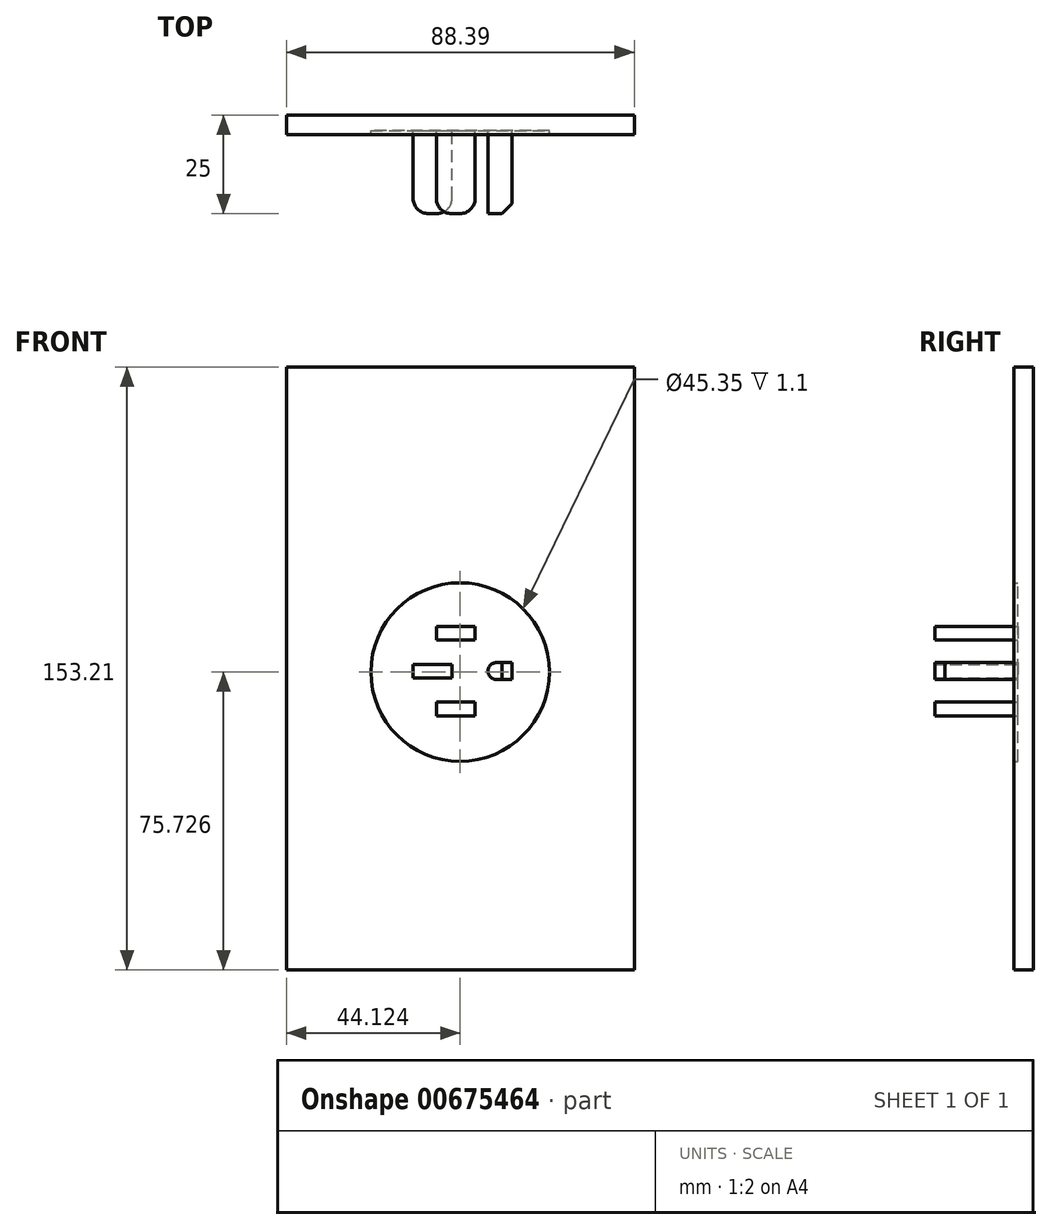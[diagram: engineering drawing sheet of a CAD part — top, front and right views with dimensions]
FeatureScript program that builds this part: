
annotation { "Feature Type Name" : "Feature", "Feature Type Description" : "" }
export const myFeature = defineFeature(function(context is Context, id is Id, definition is map)
    precondition{}
    {
        {
            var Q0;
            Q0=qCreatedBy(makeId("Front.planeOp"),FACE);
            var sketch = newSketch(context, id + "F0", { "sketchPlane" : qUnion([Q0])});
            skLineSegment(sketch, "E0.bottom", {"start": v(-39.21, 77.32) * mm, "end": v(49.18, 77.32) * mm});
            skLineSegment(sketch, "E0.top", {"start": v(-39.21, -75.89) * mm, "end": v(49.18, -75.89) * mm});
            skLineSegment(sketch, "E0.left", {"start": v(-39.21, 77.32) * mm, "end": v(-39.21, -75.89) * mm});
            skLineSegment(sketch, "E0.right", {"start": v(49.18, 77.32) * mm, "end": v(49.18, -75.89) * mm});
            skCircle(sketch, "E1", {"center": v(4.91, -0.16) * mm, "radius": 22.67 * mm});
            skLineSegment(sketch, "E2.bottom", {"start": v(-1.14, -11.26) * mm, "end": v(-1.14, -7.82) * mm});
            skLineSegment(sketch, "E2.top", {"start": v(8.73, -11.26) * mm, "end": v(8.73, -7.82) * mm});
            skLineSegment(sketch, "E2.left", {"start": v(-1.14, -11.26) * mm, "end": v(8.73, -11.26) * mm});
            skLineSegment(sketch, "E2.right", {"start": v(-1.14, -7.82) * mm, "end": v(8.73, -7.82) * mm});
            skLineSegment(sketch, "E3.MirrorCS", {"start": v(-7.02, -1.65) * mm, "end": v(2.85, -1.65) * mm});
            skLineSegment(sketch, "E4.MirrorCS", {"start": v(-1.14, 7.96) * mm, "end": v(8.73, 7.96) * mm});
            skLineSegment(sketch, "E5.MirrorCS", {"start": v(-1.14, 11.4) * mm, "end": v(-1.14, 7.96) * mm});
            skLineSegment(sketch, "E6.MirrorCS", {"start": v(-1.14, 11.4) * mm, "end": v(8.73, 11.4) * mm});
            skLineSegment(sketch, "E7.MirrorCS", {"start": v(8.73, 11.4) * mm, "end": v(8.73, 7.96) * mm});
            skLineSegment(sketch, "E8.MirrorCS", {"start": v(-7.02, 1.79) * mm, "end": v(2.85, 1.79) * mm});
            skLineSegment(sketch, "E9", {"start": v(-7.02, -1.65) * mm, "end": v(-7.02, 1.79) * mm});
            skLineSegment(sketch, "E10", {"start": v(2.85, -1.65) * mm, "end": v(2.85, 1.79) * mm});
            skLineSegment(sketch, "E11.bottom", {"start": v(18.11, -2.07) * mm, "end": v(18.11, 2.22) * mm});
            skLineSegment(sketch, "E11.left", {"start": v(18.11, -2.07) * mm, "end": v(14.12, -2.07) * mm});
            skLineSegment(sketch, "E11.right", {"start": v(18.11, 2.22) * mm, "end": v(14.12, 2.22) * mm});
            skArc(sketch, "E12", {"start": v(14.12, 2.22) * mm, "mid": v(11.97, 0.07) * mm, "end": v(14.12, -2.07) * mm});
            skSolve(sketch);
        }
        {
            var Q0;
            Q0=makeQuery(id+"F0.imprint","IMPRINT",FACE,{"disambiguationData":[TD([[makeQuery(id+"F0.imprint","IMPRINT",EDGE,{"derivedFrom":sQuery(id+"F0.wireOp",EDGE,"E0.bottom")}),-1.0]])]});
            extrude(context, id + "F1", {"entities" : qUnion([Q0]), "depth" : 5 * mm, "offsetDistance" : 25 * mm});
        }
        {
            var Q0;
            Q0=makeQuery(id+"F0.imprint","IMPRINT",FACE,{"disambiguationData":[TD([[makeQuery(id+"F0.imprint","IMPRINT",EDGE,{"derivedFrom":sQuery(id+"F0.wireOp",EDGE,"d919d92a-e6f7-40fd-a133-639b44a9ff66.bottom")}),1.0]])]});
            var Q1;
            Q1=makeQuery(id+"F0.imprint","IMPRINT",FACE,{"disambiguationData":[TD([[makeQuery(id+"F0.imprint","IMPRINT",EDGE,{"derivedFrom":sQuery(id+"F0.wireOp",EDGE,"E1")}),1.0]])]});
            extrude(context, id + "F2", {"entities" : qUnion([Q0, Q1]), "operationType" : NewBodyOperationType.ADD, "depth" : 3.9 * mm, "offsetDistance" : 25 * mm});
        }
        {
            var Q0;
            Q0=makeQuery(id+"F0.imprint","IMPRINT",FACE,{"disambiguationData":[TD([[makeQuery(id+"F0.imprint","IMPRINT",EDGE,{"derivedFrom":sQuery(id+"F0.wireOp",EDGE,"92b3ff77-899c-4692-b596-e14258b6b191")}),1.0]])]});
            var Q1;
            Q1=makeQuery(id+"F0.imprint","IMPRINT",FACE,{"disambiguationData":[TD([[makeQuery(id+"F0.imprint","IMPRINT",EDGE,{"derivedFrom":sQuery(id+"F0.wireOp",EDGE,"f2a1dbcd-aa5e-4286-995f-65eb86ff6750.MirrorCS")}),-1.0]])]});
            var Q2;
            Q2=makeQuery(id+"F0.imprint","IMPRINT",FACE,{"disambiguationData":[TD([[makeQuery(id+"F0.imprint","IMPRINT",EDGE,{"derivedFrom":sQuery(id+"F0.wireOp",EDGE,"d919d92a-e6f7-40fd-a133-639b44a9ff66.bottom")}),-1.0]])]});
            var Q3;
            Q3=makeQuery(id+"F0.imprint","IMPRINT",FACE,{"disambiguationData":[TD([[makeQuery(id+"F0.imprint","IMPRINT",EDGE,{"derivedFrom":sQuery(id+"F0.wireOp",EDGE,"E2.bottom")}),-1.0]])]});
            var Q4;
            Q4=makeQuery(id+"F0.imprint","IMPRINT",FACE,{"disambiguationData":[TD([[makeQuery(id+"F0.imprint","IMPRINT",EDGE,{"derivedFrom":sQuery(id+"F0.wireOp",EDGE,"E3.MirrorCS")}),1.0]])]});
            var Q5;
            Q5=makeQuery(id+"F0.imprint","IMPRINT",FACE,{"disambiguationData":[TD([[makeQuery(id+"F0.imprint","IMPRINT",EDGE,{"derivedFrom":sQuery(id+"F0.wireOp",EDGE,"E4.MirrorCS")}),1.0]])]});
            var Q6;
            Q6=makeQuery(id+"F0.imprint","IMPRINT",FACE,{"disambiguationData":[TD([[makeQuery(id+"F0.imprint","IMPRINT",EDGE,{"derivedFrom":sQuery(id+"F0.wireOp",EDGE,"E11.bottom")}),1.0]])]});
            extrude(context, id + "F3", {"entities" : qUnion([Q0, Q1, Q2, Q3, Q4, Q5, Q6]), "operationType" : NewBodyOperationType.ADD, "depth" : 25 * mm, "offsetDistance" : 25 * mm});
        }
        {
            var Q0;
            Q0=makeQuery(id+"F3.opExtrude","CAP_EDGE",EDGE,{"disambiguationData":[OSD([sQuery(id+"F0.wireOp",EDGE,"E2.bottom")])],"isStart":false});
            var Q1;
            Q1=makeQuery(id+"F3.opExtrude","CAP_EDGE",EDGE,{"disambiguationData":[OSD([sQuery(id+"F0.wireOp",EDGE,"E2.top")])],"isStart":false});
            var Q2;
            Q2=makeQuery(id+"F3.opExtrude","CAP_EDGE",EDGE,{"disambiguationData":[OSD([sQuery(id+"F0.wireOp",EDGE,"E9")])],"isStart":false});
            var Q3;
            Q3=makeQuery(id+"F3.opExtrude","CAP_EDGE",EDGE,{"disambiguationData":[OSD([sQuery(id+"F0.wireOp",EDGE,"E10")])],"isStart":false});
            var Q4;
            Q4=makeQuery(id+"F3.opExtrude","CAP_EDGE",EDGE,{"disambiguationData":[OSD([sQuery(id+"F0.wireOp",EDGE,"E7.MirrorCS")])],"isStart":false});
            var Q5;
            Q5=makeQuery(id+"F3.opExtrude","CAP_EDGE",EDGE,{"disambiguationData":[OSD([sQuery(id+"F0.wireOp",EDGE,"E5.MirrorCS")])],"isStart":false});
            fillet(context, id + "F4", {"entities" : qUnion([Q0, Q1, Q2, Q3, Q4, Q5]), "radius" : 3.86 * mm, "tangentPropagation" : true, "allowEdgeOverflow" : false});
        }
        {
            var Q0;
            Q0=makeQuery(id+"F3.opExtrude","CAP_EDGE",EDGE,{"disambiguationData":[OSD([sQuery(id+"F0.wireOp",EDGE,"E11.bottom")])],"isStart":false});
            chamfer(context, id + "F5", {"entities" : qUnion([Q0]), "width" : 2.5 * mm, "tangentPropagation" : true});
        }
    });
